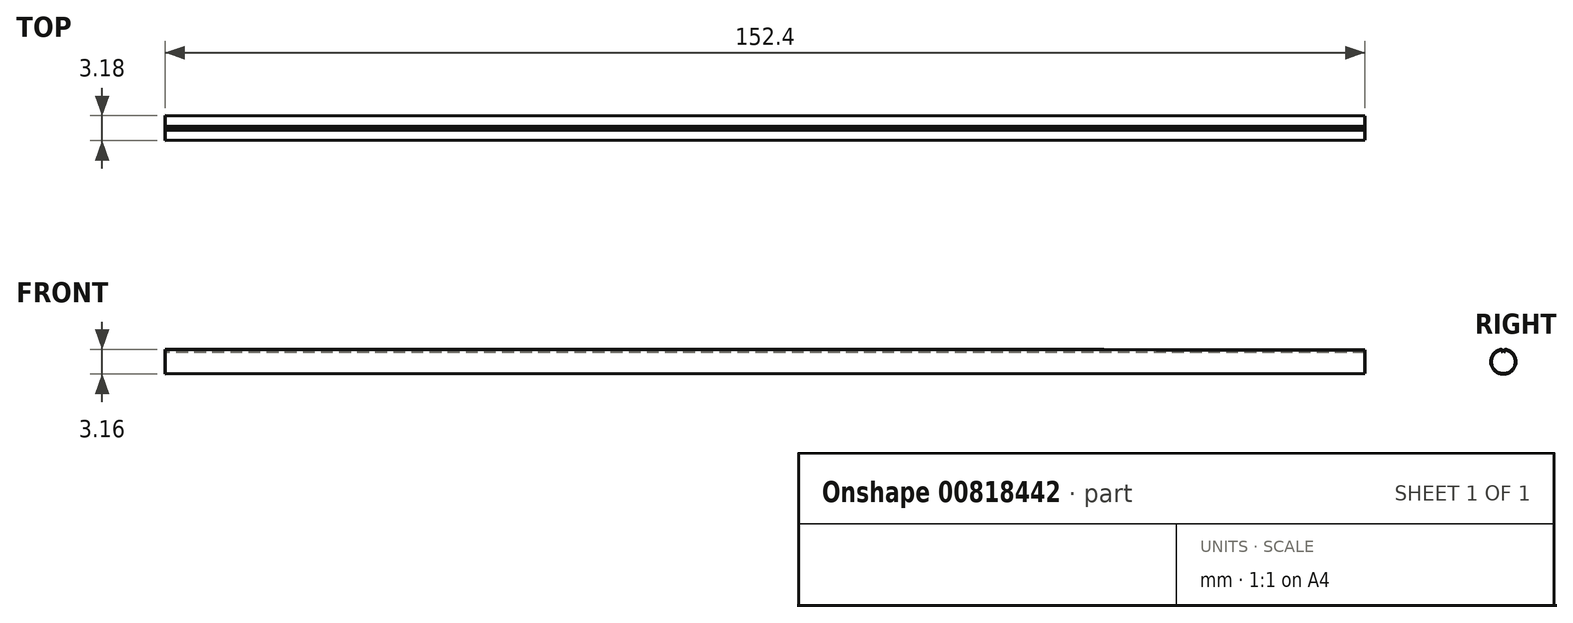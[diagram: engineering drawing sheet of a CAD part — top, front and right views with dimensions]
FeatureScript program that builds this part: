
annotation { "Feature Type Name" : "Feature", "Feature Type Description" : "" }
export const myFeature = defineFeature(function(context is Context, id is Id, definition is map)
    precondition{}
    {
        {
            var Q0;
            Q0=qCreatedBy(makeId("Right.planeOp"),FACE);
            var sketch = newSketch(context, id + "F0", { "sketchPlane" : qUnion([Q0])});
            skCircle(sketch, "E0", {"center": v(0, 0) * mm, "radius": 1.59 * mm});
            skSolve(sketch);
        }
        {
            var Q0;
            Q0=qCreatedBy(makeId("Right.planeOp"),FACE);
            cPlane(context, id + "F1", {"entities" : qUnion([Q0]), "cplaneType" : CPlaneType.OFFSET, "offset" : 152.4 * mm, "width" : 152.4 * mm, "height" : 152.4 * mm});
        }
        {
            var Q0;
            Q0=qCreatedBy(id+"F1.planeOp",FACE);
            var sketch = newSketch(context, id + "F2", { "sketchPlane" : qUnion([Q0])});
            skCircle(sketch, "E1", {"center": v(0, 0) * mm, "radius": 1.52 * mm});
            skSolve(sketch);
        }
        {
            var Q0;
            Q0=makeQuery(id+"F0.imprint","IMPRINT",FACE,{"disambiguationData":[TD([[makeQuery(id+"F0.imprint","IMPRINT",EDGE,{"derivedFrom":sQuery(id+"F0.wireOp",EDGE,"E0")}),1.0]])]});
            var Q1;
            Q1=makeQuery(id+"F2.imprint","IMPRINT",FACE,{"disambiguationData":[TD([[makeQuery(id+"F2.imprint","IMPRINT",EDGE,{"derivedFrom":sQuery(id+"F2.wireOp",EDGE,"E1")}),1.0]])]});
            loft(context, id + "F3", {"sheetProfilesArray" : [{ "sheetProfileEntities" : qUnion([Q0]) }, { "sheetProfileEntities" : qUnion([Q1]) }]});
        }
        {
            var Q0;
            Q0=makeQuery(id+"F3.opLoft","CAP_FACE",FACE,{"disambiguationData":[OSD([makeQuery(id+"F0.imprint","IMPRINT",FACE,{"disambiguationData":[TD([[makeQuery(id+"F0.imprint","IMPRINT",EDGE,{"derivedFrom":sQuery(id+"F0.wireOp",EDGE,"E0")}),1.0]])]})])],"isStart":true});
            var sketch = newSketch(context, id + "F4", { "sketchPlane" : qUnion([Q0])});
            skCircle(sketch, "E2.cCircle", {"center": v(0, 0) * mm, "radius": 1.59 * mm, "construction": true});
            skLineSegment(sketch, "E2.0", {"start": v(1.58, -0.12) * mm, "end": v(1.48, -0.58) * mm, "construction": true});
            skLineSegment(sketch, "E2.1", {"start": v(1.48, -0.58) * mm, "end": v(1.24, -0.99) * mm, "construction": true});
            skLineSegment(sketch, "E2.2", {"start": v(1.24, -0.99) * mm, "end": v(0.9, -1.31) * mm, "construction": true});
            skLineSegment(sketch, "E2.3", {"start": v(0.9, -1.31) * mm, "end": v(0.47, -1.52) * mm, "construction": true});
            skLineSegment(sketch, "E2.4", {"start": v(0.47, -1.52) * mm, "end": v(0, -1.59) * mm, "construction": true});
            skLineSegment(sketch, "E2.5", {"start": v(0, -1.59) * mm, "end": v(-0.47, -1.52) * mm, "construction": true});
            skLineSegment(sketch, "E2.6", {"start": v(-0.47, -1.52) * mm, "end": v(-0.9, -1.31) * mm, "construction": true});
            skLineSegment(sketch, "E2.7", {"start": v(-0.9, -1.31) * mm, "end": v(-1.24, -0.99) * mm, "construction": true});
            skLineSegment(sketch, "E2.8", {"start": v(-1.24, -0.99) * mm, "end": v(-1.48, -0.58) * mm, "construction": true});
            skLineSegment(sketch, "E2.9", {"start": v(-1.48, -0.58) * mm, "end": v(-1.58, -0.12) * mm, "construction": true});
            skLineSegment(sketch, "E2.10", {"start": v(-1.58, -0.12) * mm, "end": v(-1.55, 0.35) * mm, "construction": true});
            skLineSegment(sketch, "E2.11", {"start": v(-1.55, 0.35) * mm, "end": v(-1.37, 0.8) * mm, "construction": true});
            skLineSegment(sketch, "E2.12", {"start": v(-1.37, 0.8) * mm, "end": v(-1.08, 1.16) * mm, "construction": true});
            skLineSegment(sketch, "E2.13", {"start": v(-1.08, 1.16) * mm, "end": v(-0.69, 1.43) * mm, "construction": true});
            skLineSegment(sketch, "E2.14", {"start": v(-0.69, 1.43) * mm, "end": v(-0.24, 1.57) * mm, "construction": true});
            skLineSegment(sketch, "E2.15", {"start": v(-0.24, 1.57) * mm, "end": v(0.24, 1.57) * mm, "construction": true});
            skLineSegment(sketch, "E2.16", {"start": v(0.24, 1.57) * mm, "end": v(0.69, 1.43) * mm, "construction": true});
            skLineSegment(sketch, "E2.17", {"start": v(0.69, 1.43) * mm, "end": v(1.08, 1.16) * mm, "construction": true});
            skLineSegment(sketch, "E2.18", {"start": v(1.08, 1.16) * mm, "end": v(1.37, 0.8) * mm, "construction": true});
            skLineSegment(sketch, "E2.19", {"start": v(1.37, 0.8) * mm, "end": v(1.55, 0.35) * mm, "construction": true});
            skLineSegment(sketch, "E2.20", {"start": v(1.55, 0.35) * mm, "end": v(1.58, -0.12) * mm, "construction": true});
            skLineSegment(sketch, "E3", {"start": v(-0.24, 1.57) * mm, "end": v(0, 1.16) * mm});
            skLineSegment(sketch, "E4", {"start": v(0, 1.16) * mm, "end": v(0.24, 1.57) * mm});
            skArc(sketch, "E5", {"start": v(0.22, 1.57) * mm, "mid": v(0, 1.59) * mm, "end": v(-0.24, 1.57) * mm});
            skSolve(sketch);
        }
        {
            var Q0;
            Q0=makeQuery(id+"F4.imprint","IMPRINT",FACE,{"disambiguationData":[TD([[makeQuery(id+"F4.imprint","IMPRINT",EDGE,{"derivedFrom":sQuery(id+"F4.wireOp",EDGE,"E3")}),1.0]])]});
            extrude(context, id + "F5", {"entities" : qUnion([Q0]), "operationType" : NewBodyOperationType.REMOVE, "endBound" : BoundingType.THROUGH_ALL, "oppositeDirection" : true, "depth" : 25.4 * mm, "offsetDistance" : 25.4 * mm});
        }
    });
